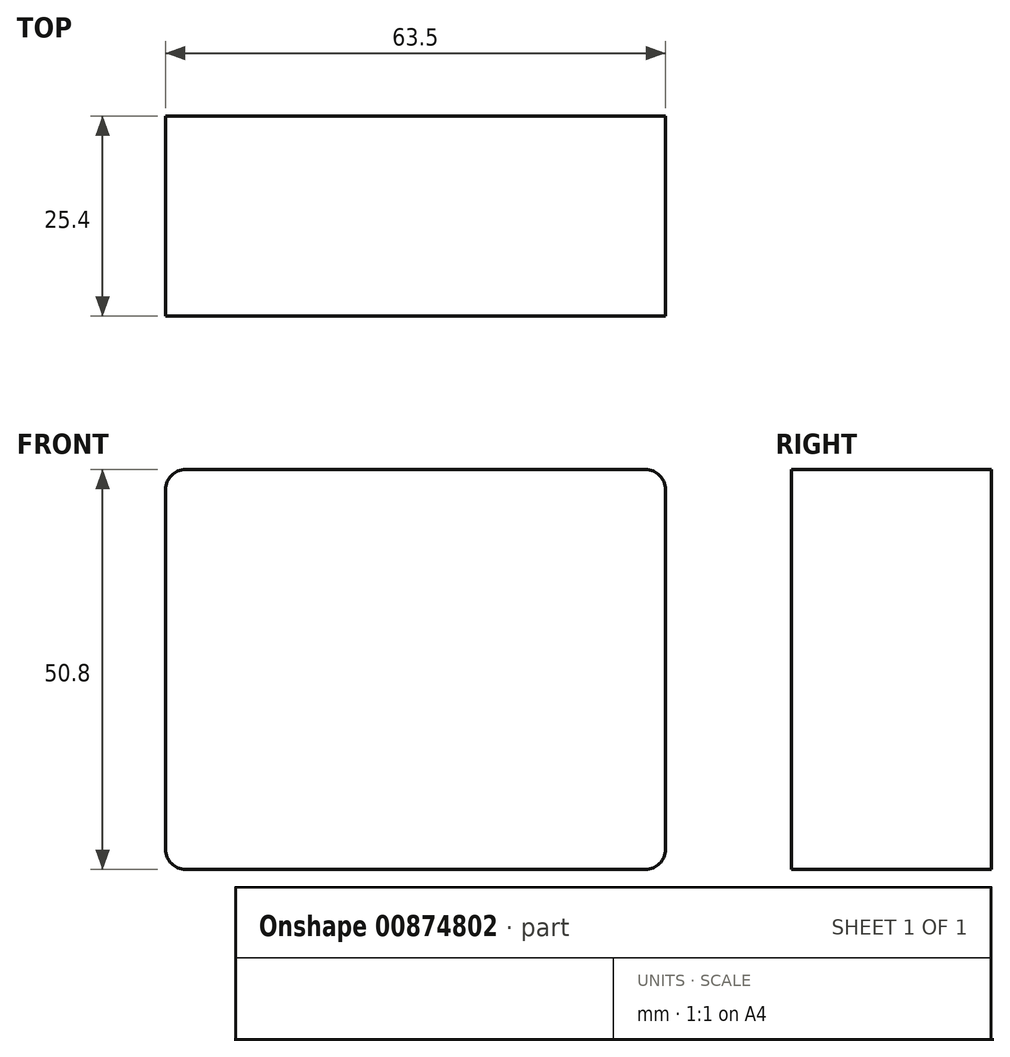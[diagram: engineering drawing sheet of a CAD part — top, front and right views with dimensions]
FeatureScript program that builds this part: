
annotation { "Feature Type Name" : "Feature", "Feature Type Description" : "" }
export const myFeature = defineFeature(function(context is Context, id is Id, definition is map)
    precondition{}
    {
        {
            var Q0;
            Q0=qCreatedBy(makeId("Front.planeOp"),FACE);
            var sketch = newSketch(context, id + "F0", { "sketchPlane" : qUnion([Q0])});
            skLineSegment(sketch, "E0.bottom", {"start": v(29.2, 25.4) * mm, "end": v(-29.21, 25.4) * mm});
            skLineSegment(sketch, "E0.top", {"start": v(29.21, -25.4) * mm, "end": v(-29.2, -25.4) * mm});
            skLineSegment(sketch, "E0.left", {"start": v(31.75, 22.86) * mm, "end": v(31.75, -22.86) * mm});
            skLineSegment(sketch, "E0.right", {"start": v(-31.75, 22.86) * mm, "end": v(-31.75, -22.86) * mm});
            skPoint(sketch, "E0.middle", {"position": v(0, 0) * mm});
            skPoint(sketch, "E1.visualSharp", {"position": v(-31.75, 25.4) * mm});
            skArc(sketch, "E1.filletArc", {"start": v(-29.21, 25.4) * mm, "mid": v(-31, 24.66) * mm, "end": v(-31.75, 22.86) * mm});
            skPoint(sketch, "E2.visualSharp", {"position": v(-31.75, -25.4) * mm});
            skArc(sketch, "E2.filletArc", {"start": v(-31.75, -22.86) * mm, "mid": v(-31, -24.66) * mm, "end": v(-29.2, -25.4) * mm});
            skPoint(sketch, "E3.visualSharp", {"position": v(31.75, -25.4) * mm});
            skArc(sketch, "E3.filletArc", {"start": v(29.21, -25.4) * mm, "mid": v(31, -24.66) * mm, "end": v(31.75, -22.86) * mm});
            skPoint(sketch, "E4.visualSharp", {"position": v(31.75, 25.4) * mm});
            skArc(sketch, "E4.filletArc", {"start": v(31.75, 22.86) * mm, "mid": v(31, 24.66) * mm, "end": v(29.2, 25.4) * mm});
            skSolve(sketch);
        }
        {
            var Q0;
            Q0 = qSketchRegion(id + "F0", true);
            extrude(context, id + "F1", {"entities" : qUnion([Q0]), "depth" : 25.4 * mm, "offsetDistance" : 25.4 * mm});
        }
    });
